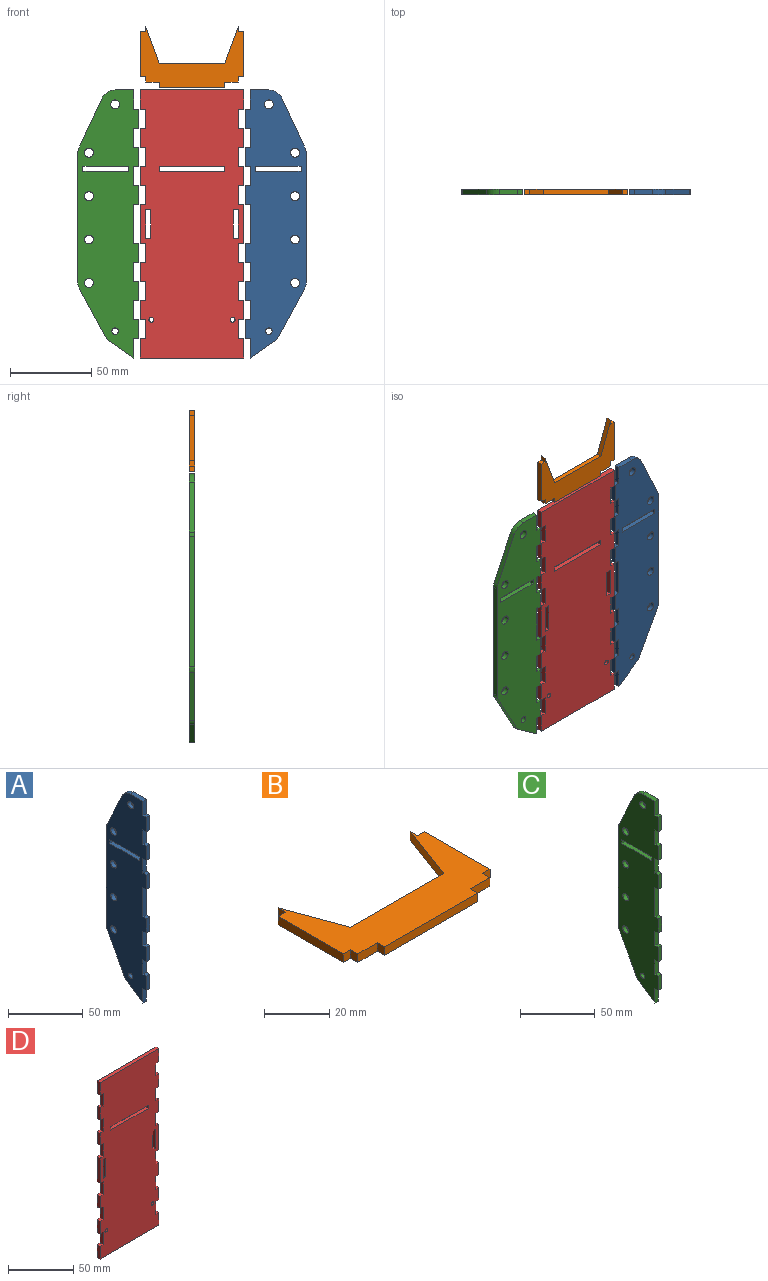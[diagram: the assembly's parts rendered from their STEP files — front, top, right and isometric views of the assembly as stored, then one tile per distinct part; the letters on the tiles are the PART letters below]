
ASSEMBLY  parts=4 mates=7
PART A: 46 faces, bbox 3.2x37.7x165.1 mm
  f0: plane 165.1x37.67mm, normal (1,0,0), area 4771.6mm2, adj f1,f2,f3,f4,f5,f6,f7,f8
  f1: plane 11.76x3.18mm, normal (0,-1,0), area 37.3mm2, adj f0,f2,f32,f35
  f2: plane 3.18x3.18mm, normal (0,0,1), area 10.1mm2, adj f0,f1,f3,f32
  f3: plane 11.76x3.18mm, normal (0,-1,0), area 37.3mm2, adj f0,f2,f4,f32
  f4: plane 3.18x3.18mm, normal (0,0,-1), area 10.1mm2, adj f0,f3,f5,f32
  f5: plane 11.76x3.18mm, normal (0,-1,0), area 37.3mm2, adj f0,f4,f6,f32
  f6: plane 15.45x10.91mm, normal (0,0.58,-0.82), area 60.1mm2, adj f0,f5,f7,f32
  f7: cylinder r=6.86mm len=3.18mm, axis (-1,0,0), area 10mm2, adj f0,f6,f8,f32
  f8: plane 29.77x16.14mm, normal (0,0.88,-0.48), area 107.5mm2, adj f0,f7,f9,f32
  f9: cylinder r=6.86mm len=3.27mm, axis (-1,0,0), area 10.8mm2, adj f0,f8,f10,f32
  f10: plane 80.15x3.18mm, normal (0,1,0), area 254.5mm2, adj f0,f9,f11,f32
  f11: cylinder r=6.86mm len=3.18mm, axis (-1,0,0), area 9.5mm2, adj f0,f10,f12,f32
  f12: plane 30.63x14.3mm, normal (0,0.91,0.42), area 107.3mm2, adj f0,f11,f13,f32
  f13: cylinder r=8.89mm len=8.06mm, axis (-1,0,0), area 32mm2, adj f0,f12,f14,f32
  f14: plane 11.5x3.18mm, normal (0,0,1), area 36.5mm2, adj f0,f13,f15,f32
  f15: plane 11.76x3.18mm, normal (0,-1,0), area 37.3mm2, adj f0,f14,f16,f32
  f16: plane 3.18x3.18mm, normal (0,0,1), area 10.1mm2, adj f0,f15,f17,f32
  f17: plane 11.76x3.18mm, normal (0,-1,0), area 37.3mm2, adj f0,f16,f18,f32
  f18: plane 3.18x3.18mm, normal (0,0,-1), area 10.1mm2, adj f0,f17,f19,f32
  f19: plane 11.76x3.18mm, normal (0,-1,0), area 37.3mm2, adj f0,f18,f20,f32
  f20: plane 3.18x3.18mm, normal (0,0,1), area 10.1mm2, adj f0,f19,f21,f32
  f21: plane 11.76x3.18mm, normal (0,-1,0), area 37.3mm2, adj f0,f20,f22,f32
  f22: plane 3.18x3.18mm, normal (0,0,-1), area 10.1mm2, adj f0,f21,f23,f32
  f23: plane 11.76x3.18mm, normal (0,-1,0), area 37.3mm2, adj f0,f22,f24,f32
  f24: plane 3.18x3.18mm, normal (0,0,1), area 10.1mm2, adj f0,f23,f25,f32
  f25: plane 11.76x3.18mm, normal (0,-1,0), area 37.3mm2, adj f0,f24,f26,f32
  f26: plane 3.18x3.18mm, normal (0,0,-1), area 10.1mm2, adj f0,f25,f27,f32
  f27: plane 24.04x3.18mm, normal (0,-1,0), area 76.3mm2, adj f0,f26,f28,f32
  f28: plane 3.18x3.18mm, normal (0,0,1), area 10.1mm2, adj f0,f27,f29,f32
  f29: plane 11.76x3.18mm, normal (0,-1,0), area 37.3mm2, adj f0,f28,f30,f32
  f30: plane 3.18x3.18mm, normal (0,0,-1), area 10.1mm2, adj f0,f29,f31,f32
  f31: plane 11.76x3.18mm, normal (0,-1,0), area 37.3mm2, adj f0,f30,f32,f34
  f32: plane 165.1x37.67mm, normal (-1,0,0), area 4771.6mm2, adj f1,f2,f3,f4,f5,f6,f7,f8
  f33: cylinder r=2.75mm len=5.5mm, axis (-1,0,0), area 54.9mm2, adj f0,f32
  f34: plane 3.18x3.18mm, normal (0,0,1), area 10.1mm2, adj f0,f31,f32,f36
  f35: plane 3.18x3.18mm, normal (0,0,-1), area 10.1mm2, adj f0,f1,f32,f36
  f36: plane 11.76x3.18mm, normal (0,-1,0), area 37.3mm2, adj f0,f32,f34,f35
  f37: cylinder r=2.75mm len=5.5mm, axis (-1,0,0), area 54.9mm2, adj f0,f32
  f38: cylinder r=2mm len=4mm, axis (-1,0,0), area 39.9mm2, adj f0,f32
  f39: cylinder r=2.75mm len=5.5mm, axis (-1,0,0), area 54.9mm2, adj f0,f32
  f40: cylinder r=2.75mm len=5.5mm, axis (-1,0,0), area 54.9mm2, adj f0,f32
  f41: cylinder r=2.75mm len=5.5mm, axis (-1,0,0), area 54.9mm2, adj f0,f32
  f42: plane 28.15x3.18mm, normal (0,0,1), area 89.4mm2, adj f0,f32,f44,f45
  f43: plane 28.15x3.18mm, normal (0,0,-1), area 89.4mm2, adj f0,f32,f44,f45
  f44: plane 3.18x3.18mm, normal (0,1,0), area 10.1mm2, adj f0,f32,f42,f43
  f45: plane 3.18x3.18mm, normal (0,-1,0), area 10.1mm2, adj f0,f32,f42,f43
PART B: 20 faces, bbox 63.5x37.7x3.2 mm
  f0: plane 63.5x37.67mm, normal (0,0,-1), area 1158.4mm2, adj f2,f3,f4,f5,f6,f7,f8,f9
  f1: plane 63.5x37.67mm, normal (0,0,1), area 1158.4mm2, adj f2,f3,f4,f5,f6,f7,f8,f9
  f2: plane 23x8.47mm, normal (0.94,0.35,0), area 77.8mm2, adj f0,f1,f3,f18
  f3: plane 3.18x3.18mm, normal (-1,0,0), area 10.1mm2, adj f0,f1,f2,f4
  f4: plane 3.18x3.18mm, normal (0,1,0), area 10.1mm2, adj f0,f1,f3,f5
  f5: plane 28.15x3.18mm, normal (-1,0,0), area 89.4mm2, adj f0,f1,f4,f6
  f6: plane 3.18x3.18mm, normal (0,-1,0), area 10.1mm2, adj f0,f1,f5,f7
  f7: plane 3.18x3.18mm, normal (-1,0,0), area 10.1mm2, adj f0,f1,f6,f8
  f8: plane 8.47x3.18mm, normal (0,-1,0), area 26.9mm2, adj f0,f1,f7,f9
  f9: plane 3.18x3.18mm, normal (-1,0,0), area 10.1mm2, adj f0,f1,f8,f10
  f10: plane 40.22x3.18mm, normal (0,-1,0), area 127.7mm2, adj f0,f1,f9,f11
  f11: plane 3.18x3.18mm, normal (1,0,0), area 10.1mm2, adj f0,f1,f10,f12
  f12: plane 8.47x3.18mm, normal (0,-1,0), area 26.9mm2, adj f0,f1,f11,f13
  f13: plane 3.18x3.18mm, normal (1,0,0), area 10.1mm2, adj f0,f1,f12,f14
  f14: plane 3.18x3.18mm, normal (0,-1,0), area 10.1mm2, adj f0,f1,f13,f15
  f15: plane 28.15x3.18mm, normal (1,0,0), area 89.4mm2, adj f0,f1,f14,f16
  f16: plane 3.18x3.18mm, normal (0,1,0), area 10.1mm2, adj f0,f1,f15,f17
  f17: plane 3.18x3.18mm, normal (1,0,0), area 10.1mm2, adj f0,f1,f16,f19
  f18: plane 40.22x3.18mm, normal (0,1,0), area 127.7mm2, adj f0,f1,f2,f19
  f19: plane 23x8.47mm, normal (-0.94,0.35,0), area 77.8mm2, adj f0,f1,f17,f18
PART C: 46 faces, bbox 3.2x37.7x165.1 mm
  f0: plane 165.1x37.67mm, normal (-1,0,0), area 4771.6mm2, adj f1,f2,f3,f4,f5,f6,f7,f8
  f1: plane 11.76x3.18mm, normal (0,-1,0), area 37.3mm2, adj f0,f2,f32,f35
  f2: plane 3.18x3.18mm, normal (0,0,1), area 10.1mm2, adj f0,f1,f3,f32
  f3: plane 11.76x3.18mm, normal (0,-1,0), area 37.3mm2, adj f0,f2,f4,f32
  f4: plane 3.18x3.18mm, normal (0,0,-1), area 10.1mm2, adj f0,f3,f5,f32
  f5: plane 11.76x3.18mm, normal (0,-1,0), area 37.3mm2, adj f0,f4,f6,f32
  f6: plane 15.45x10.91mm, normal (0,0.58,-0.82), area 60.1mm2, adj f0,f5,f7,f32
  f7: cylinder r=6.86mm len=3.18mm, axis (1,0,0), area 10mm2, adj f0,f6,f8,f32
  f8: plane 29.77x16.14mm, normal (0,0.88,-0.48), area 107.5mm2, adj f0,f7,f9,f32
  f9: cylinder r=6.86mm len=3.27mm, axis (1,0,0), area 10.8mm2, adj f0,f8,f10,f32
  f10: plane 80.15x3.18mm, normal (0,1,0), area 254.5mm2, adj f0,f9,f11,f32
  f11: cylinder r=6.86mm len=3.18mm, axis (1,0,0), area 9.5mm2, adj f0,f10,f12,f32
  f12: plane 30.63x14.3mm, normal (0,0.91,0.42), area 107.3mm2, adj f0,f11,f13,f32
  f13: cylinder r=8.89mm len=8.06mm, axis (1,0,0), area 32mm2, adj f0,f12,f14,f32
  f14: plane 11.5x3.18mm, normal (0,0,1), area 36.5mm2, adj f0,f13,f15,f32
  f15: plane 11.76x3.18mm, normal (0,-1,0), area 37.3mm2, adj f0,f14,f16,f32
  f16: plane 3.18x3.18mm, normal (0,0,1), area 10.1mm2, adj f0,f15,f17,f32
  f17: plane 11.76x3.18mm, normal (0,-1,0), area 37.3mm2, adj f0,f16,f18,f32
  f18: plane 3.18x3.18mm, normal (0,0,-1), area 10.1mm2, adj f0,f17,f19,f32
  f19: plane 11.76x3.18mm, normal (0,-1,0), area 37.3mm2, adj f0,f18,f20,f32
  f20: plane 3.18x3.18mm, normal (0,0,1), area 10.1mm2, adj f0,f19,f21,f32
  f21: plane 11.76x3.18mm, normal (0,-1,0), area 37.3mm2, adj f0,f20,f22,f32
  f22: plane 3.18x3.18mm, normal (0,0,-1), area 10.1mm2, adj f0,f21,f23,f32
  f23: plane 11.76x3.18mm, normal (0,-1,0), area 37.3mm2, adj f0,f22,f24,f32
  f24: plane 3.18x3.18mm, normal (0,0,1), area 10.1mm2, adj f0,f23,f25,f32
  f25: plane 11.76x3.18mm, normal (0,-1,0), area 37.3mm2, adj f0,f24,f26,f32
  f26: plane 3.18x3.18mm, normal (0,0,-1), area 10.1mm2, adj f0,f25,f27,f32
  f27: plane 24.04x3.18mm, normal (0,-1,0), area 76.3mm2, adj f0,f26,f28,f32
  f28: plane 3.18x3.18mm, normal (0,0,1), area 10.1mm2, adj f0,f27,f29,f32
  f29: plane 11.76x3.18mm, normal (0,-1,0), area 37.3mm2, adj f0,f28,f30,f32
  f30: plane 3.18x3.18mm, normal (0,0,-1), area 10.1mm2, adj f0,f29,f31,f32
  f31: plane 11.76x3.18mm, normal (0,-1,0), area 37.3mm2, adj f0,f30,f32,f34
  f32: plane 165.1x37.67mm, normal (1,0,0), area 4771.6mm2, adj f1,f2,f3,f4,f5,f6,f7,f8
  f33: cylinder r=2.75mm len=5.5mm, axis (1,0,0), area 54.9mm2, adj f0,f32
  f34: plane 3.18x3.18mm, normal (0,0,1), area 10.1mm2, adj f0,f31,f32,f36
  f35: plane 3.18x3.18mm, normal (0,0,-1), area 10.1mm2, adj f0,f1,f32,f36
  f36: plane 11.76x3.18mm, normal (0,-1,0), area 37.3mm2, adj f0,f32,f34,f35
  f37: cylinder r=2.75mm len=5.5mm, axis (1,0,0), area 54.9mm2, adj f0,f32
  f38: cylinder r=2mm len=4mm, axis (1,0,0), area 39.9mm2, adj f0,f32
  f39: cylinder r=2.75mm len=5.5mm, axis (1,0,0), area 54.9mm2, adj f0,f32
  f40: cylinder r=2.75mm len=5.5mm, axis (1,0,0), area 54.9mm2, adj f0,f32
  f41: cylinder r=2.75mm len=5.5mm, axis (1,0,0), area 54.9mm2, adj f0,f32
  f42: plane 28.15x3.18mm, normal (0,0,1), area 89.4mm2, adj f0,f32,f44,f45
  f43: plane 28.15x3.18mm, normal (0,0,-1), area 89.4mm2, adj f0,f32,f44,f45
  f44: plane 3.18x3.18mm, normal (0,-1,0), area 10.1mm2, adj f0,f32,f42,f43
  f45: plane 3.18x3.18mm, normal (0,1,0), area 10.1mm2, adj f0,f32,f42,f43
PART D: 68 faces, bbox 63.5x3.2x165.1 mm
  f0: plane 11.76x3.18mm, normal (1,0,0), area 37.3mm2, adj f1,f58,f62,f63
  f1: plane 63.5x3.18mm, normal (0,0,1), area 201.6mm2, adj f0,f2,f62,f63
  f2: plane 11.76x3.18mm, normal (-1,0,0), area 37.3mm2, adj f1,f3,f62,f63
  f3: plane 3.18x3.18mm, normal (0,0,-1), area 10.1mm2, adj f2,f4,f62,f63
  f4: plane 11.76x3.18mm, normal (-1,0,0), area 37.3mm2, adj f3,f5,f62,f63
  f5: plane 3.18x3.18mm, normal (0,0,1), area 10.1mm2, adj f4,f6,f62,f63
  f6: plane 11.76x3.18mm, normal (-1,0,0), area 37.3mm2, adj f5,f7,f62,f63
  f7: plane 3.18x3.18mm, normal (0,0,-1), area 10.1mm2, adj f6,f8,f62,f63
  f8: plane 11.76x3.18mm, normal (-1,0,0), area 37.3mm2, adj f7,f9,f62,f63
  f9: plane 3.18x3.18mm, normal (0,0,1), area 10.1mm2, adj f8,f10,f62,f63
  f10: plane 11.76x3.18mm, normal (-1,0,0), area 37.3mm2, adj f9,f11,f62,f63
  f11: plane 3.18x3.18mm, normal (0,0,-1), area 10.1mm2, adj f10,f12,f62,f63
  f12: plane 11.76x3.18mm, normal (-1,0,0), area 37.3mm2, adj f11,f13,f62,f63
  f13: plane 3.18x3.18mm, normal (0,0,1), area 10.1mm2, adj f12,f14,f62,f63
  f14: plane 24.04x3.18mm, normal (-1,0,0), area 76.3mm2, adj f13,f15,f62,f63
  f15: plane 3.18x3.18mm, normal (0,0,-1), area 10.1mm2, adj f14,f16,f62,f63
  f16: plane 11.76x3.18mm, normal (-1,0,0), area 37.3mm2, adj f15,f17,f62,f63
  f17: plane 3.18x3.18mm, normal (0,0,1), area 10.1mm2, adj f16,f18,f62,f63
  f18: plane 11.76x3.18mm, normal (-1,0,0), area 37.3mm2, adj f17,f19,f62,f63
  f19: plane 3.18x3.18mm, normal (0,0,-1), area 10.1mm2, adj f18,f20,f62,f63
  f20: plane 11.76x3.18mm, normal (-1,0,0), area 37.3mm2, adj f19,f21,f62,f63
  f21: plane 3.18x3.18mm, normal (0,0,1), area 10.1mm2, adj f20,f22,f62,f63
  f22: plane 11.76x3.18mm, normal (-1,0,0), area 37.3mm2, adj f21,f23,f62,f63
  f23: plane 3.18x3.18mm, normal (0,0,-1), area 10.1mm2, adj f22,f24,f62,f63
  f24: plane 11.76x3.18mm, normal (-1,0,0), area 37.3mm2, adj f23,f25,f62,f63
  f25: plane 3.18x3.18mm, normal (0,0,1), area 10.1mm2, adj f24,f26,f62,f63
  f26: plane 11.76x3.18mm, normal (-1,0,0), area 37.3mm2, adj f25,f27,f62,f63
  f27: plane 63.5x3.18mm, normal (0,0,-1), area 201.6mm2, adj f26,f28,f62,f63
  f28: plane 11.76x3.18mm, normal (1,0,0), area 37.3mm2, adj f27,f29,f62,f63
  f29: plane 3.18x3.18mm, normal (0,0,1), area 10.1mm2, adj f28,f30,f62,f63
  f30: plane 11.76x3.18mm, normal (1,0,0), area 37.3mm2, adj f29,f31,f62,f63
  f31: plane 3.18x3.18mm, normal (0,0,-1), area 10.1mm2, adj f30,f32,f62,f63
  f32: plane 11.76x3.18mm, normal (1,0,0), area 37.3mm2, adj f31,f33,f62,f63
  f33: plane 3.18x3.18mm, normal (0,0,1), area 10.1mm2, adj f32,f34,f62,f63
  f34: plane 11.76x3.18mm, normal (1,0,0), area 37.3mm2, adj f33,f35,f62,f63
  f35: plane 3.18x3.18mm, normal (0,0,-1), area 10.1mm2, adj f34,f36,f62,f63
  f36: plane 11.76x3.18mm, normal (1,0,0), area 37.3mm2, adj f35,f37,f62,f63
  f37: plane 3.18x3.18mm, normal (0,0,1), area 10.1mm2, adj f36,f38,f62,f63
  f38: plane 11.76x3.18mm, normal (1,0,0), area 37.3mm2, adj f37,f39,f62,f63
  f39: plane 3.18x3.18mm, normal (0,0,-1), area 10.1mm2, adj f38,f40,f62,f63
  f40: plane 24.04x3.18mm, normal (1,0,0), area 76.3mm2, adj f39,f41,f62,f63
  f41: plane 3.18x3.18mm, normal (0,0,1), area 10.1mm2, adj f40,f42,f62,f63
  f42: plane 11.76x3.18mm, normal (1,0,0), area 37.3mm2, adj f41,f43,f62,f63
  f43: plane 3.18x3.18mm, normal (0,0,-1), area 10.1mm2, adj f42,f44,f62,f63
  f44: plane 11.76x3.18mm, normal (1,0,0), area 37.3mm2, adj f43,f45,f62,f63
  f45: plane 3.18x3.18mm, normal (0,0,1), area 10.1mm2, adj f44,f46,f62,f63
  f46: plane 11.76x3.18mm, normal (1,0,0), area 37.3mm2, adj f45,f47,f62,f63
  f47: plane 3.18x3.18mm, normal (0,0,-1), area 10.1mm2, adj f46,f48,f62,f63
  f48: plane 11.76x3.18mm, normal (1,0,0), area 37.3mm2, adj f47,f49,f62,f63
  f49: plane 3.18x3.18mm, normal (0,0,1), area 10.1mm2, adj f48,f50,f62,f63
  f50: plane 11.76x3.18mm, normal (1,0,0), area 37.3mm2, adj f49,f58,f62,f63
  f51: plane 3.18x3.18mm, normal (0,0,-1), area 10.1mm2, adj f52,f59,f62,f63
  f52: plane 17.69x3.18mm, normal (-1,0,0), area 56.2mm2, adj f51,f53,f62,f63
  f53: plane 3.18x3.18mm, normal (0,0,1), area 10.1mm2, adj f52,f59,f62,f63
  f54: plane 17.69x3.18mm, normal (1,0,0), area 56.2mm2, adj f55,f60,f62,f63
  f55: plane 3.18x3.18mm, normal (0,0,-1), area 10.1mm2, adj f54,f56,f62,f63
  f56: plane 17.69x3.18mm, normal (-1,0,0), area 56.2mm2, adj f55,f60,f62,f63
  f57: cylinder r=1.5mm len=3.18mm, axis (0,1,0), area 29.9mm2, adj f62,f63
  f58: plane 3.18x3.18mm, normal (0,0,-1), area 10.1mm2, adj f0,f50,f62,f63
  f59: plane 17.69x3.18mm, normal (1,0,0), area 56.2mm2, adj f51,f53,f62,f63
  f60: plane 3.18x3.18mm, normal (0,0,1), area 10.1mm2, adj f54,f56,f62,f63
  f61: cylinder r=1.5mm len=3.18mm, axis (0,1,0), area 29.9mm2, adj f62,f63
  f62: plane 165.1x63.5mm, normal (0,-1,0), area 9781.8mm2, adj f0,f1,f2,f3,f4,f5,f6,f7
  f63: plane 165.1x63.5mm, normal (0,1,0), area 9781.8mm2, adj f0,f1,f2,f3,f4,f5,f6,f7
  f64: plane 40.22x3.18mm, normal (0,0,1), area 127.7mm2, adj f62,f63,f66,f67
  f65: plane 40.22x3.18mm, normal (0,0,-1), area 127.7mm2, adj f62,f63,f66,f67
  f66: plane 3.18x3.18mm, normal (1,0,0), area 10.1mm2, adj f62,f63,f64,f65
  f67: plane 3.18x3.18mm, normal (-1,0,0), area 10.1mm2, adj f62,f63,f64,f65
PLACE A rot(axis=(0,0,-1),90deg) t=(-9.63,34.16,-13.67)mm
PLACE B rot(axis=(1,0,0),90deg) t=(-45.47,96.98,132.82)mm
PLACE C rot(axis=(0,0,1),90deg) t=(-81.31,34.16,-13.67)mm
PLACE D t=(-45.47,5.58,-13.67)mm fixed
MATE planar D.f62 <-> C.f0  axis (0,-1,0) through (-16.9,2.41,104.41)mm
MATE planar D.f1 <-> C.f14  axis (0,0,1) through (-45.47,4,127.92)mm
MATE planar B.f15 <-> D.f0  axis (1,0,0) through (-13.72,4,150.07)mm
MATE planar D.f1 <-> A.f14  axis (0,0,1) through (-45.47,4,127.92)mm
MATE planar D.f62 <-> B.f1  axis (0,-1,0) through (-45.47,2.41,45.02)mm
MATE planar D.f62 <-> A.f0  axis (0,-1,0) through (-45.47,2.41,45.02)mm
MATE parallel D.f40 <-> A.f17  axis (1,0,0) through (-13.72,4,45.37)mm
